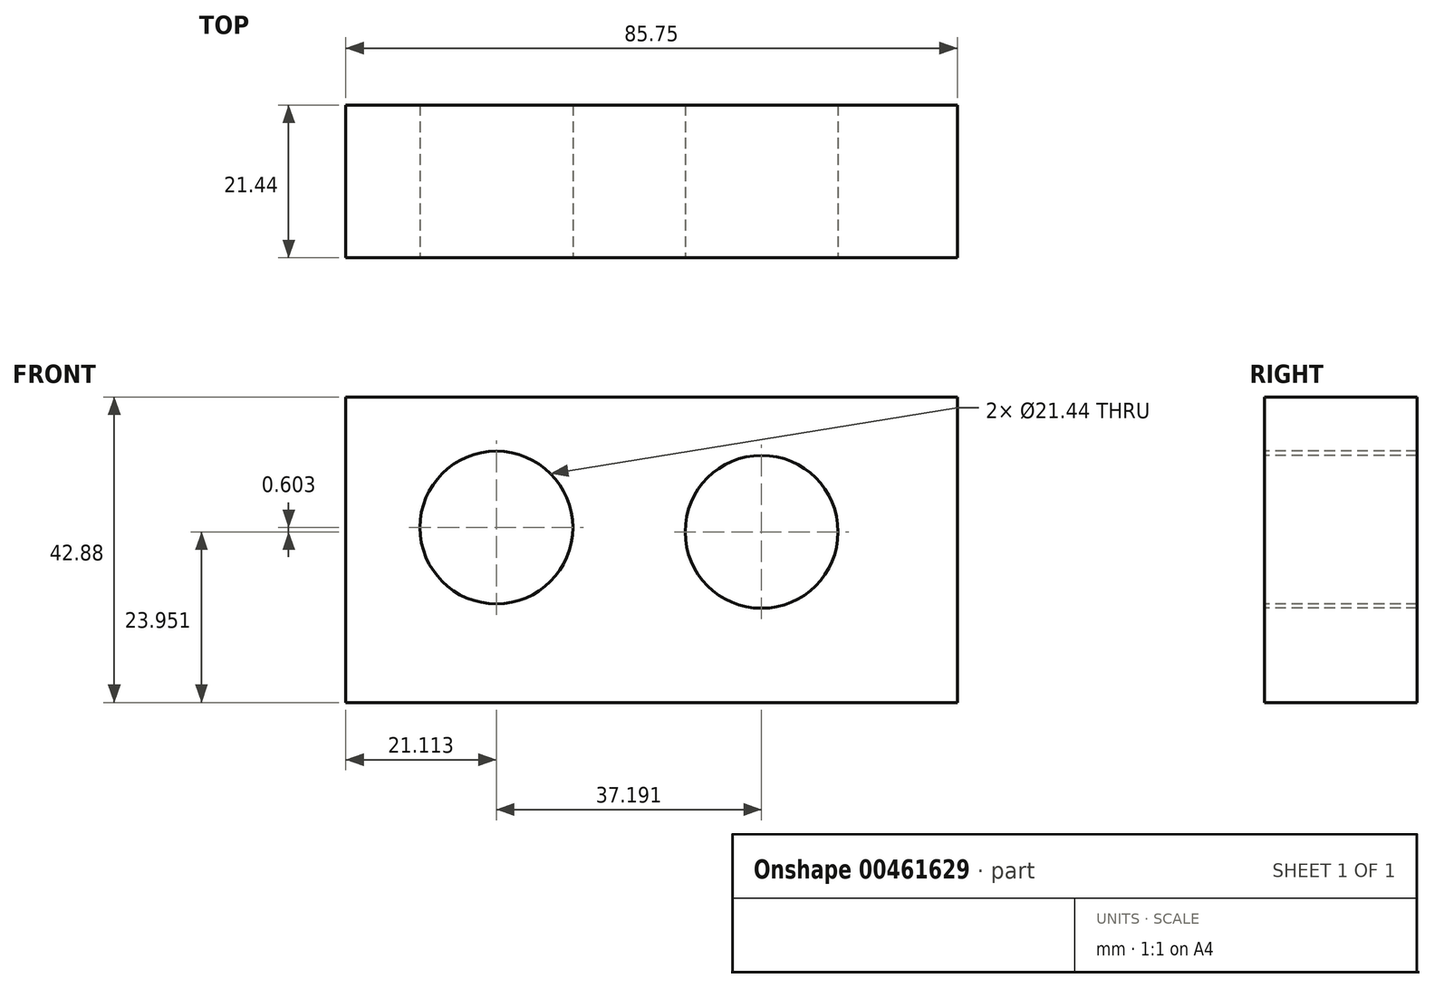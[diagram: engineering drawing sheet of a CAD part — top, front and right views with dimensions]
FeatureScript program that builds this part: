
annotation { "Feature Type Name" : "Feature", "Feature Type Description" : "" }
export const myFeature = defineFeature(function(context is Context, id is Id, definition is map)
    precondition{}
    {
        {
            var Q0;
            Q0=qCreatedBy(makeId("Front.planeOp"),FACE);
            var sketch = newSketch(context, id + "F0", { "sketchPlane" : qUnion([Q0])});
            skLineSegment(sketch, "E0.bottom", {"start": v(-34.18, 21.14) * mm, "end": v(51.57, 21.14) * mm});
            skLineSegment(sketch, "E0.top", {"start": v(-34.18, -21.74) * mm, "end": v(51.57, -21.74) * mm});
            skLineSegment(sketch, "E0.left", {"start": v(-34.18, 21.14) * mm, "end": v(-34.18, -21.74) * mm});
            skLineSegment(sketch, "E0.right", {"start": v(51.57, 21.14) * mm, "end": v(51.57, -21.74) * mm});
            skSolve(sketch);
        }
        {
            var Q0;
            Q0 = qSketchRegion(id + "F0", true);
            extrude(context, id + "F1", {"entities" : qUnion([Q0]), "depth" : 21.44 * mm});
        }
        {
            var Q0;
            Q0=makeQuery(id+"F1.opExtrude","CAP_FACE",FACE,{"disambiguationData":[OSD([sQuery(id+"F0.wireOp",EDGE,"E0.bottom"),sQuery(id+"F0.wireOp",EDGE,"E0.top"),sQuery(id+"F0.wireOp",EDGE,"E0.left"),sQuery(id+"F0.wireOp",EDGE,"E0.right")])],"isStart":false});
            var sketch = newSketch(context, id + "F2", { "sketchPlane" : qUnion([Q0])});
            skCircle(sketch, "E1", {"center": v(-13.07, 2.81) * mm, "radius": 10.72 * mm});
            skSolve(sketch);
        }
        {
            var Q0;
            Q0 = qSketchRegion(id + "F2", true);
            extrude(context, id + "F3", {"entities" : qUnion([Q0]), "operationType" : NewBodyOperationType.REMOVE, "oppositeDirection" : true, "depth" : 32.5 * mm});
        }
        {
            var Q0;
            Q0=makeQuery(id+"F1.opExtrude","CAP_FACE",FACE,{"disambiguationData":[OSD([sQuery(id+"F0.wireOp",EDGE,"E0.bottom"),sQuery(id+"F0.wireOp",EDGE,"E0.top"),sQuery(id+"F0.wireOp",EDGE,"E0.left"),sQuery(id+"F0.wireOp",EDGE,"E0.right")])],"isStart":false});
            var sketch = newSketch(context, id + "F4", { "sketchPlane" : qUnion([Q0])});
            skCircle(sketch, "E2", {"center": v(24.12, 2.21) * mm, "radius": 10.72 * mm});
            skSolve(sketch);
        }
        {
            var Q0;
            Q0 = qSketchRegion(id + "F4", true);
            extrude(context, id + "F5", {"entities" : qUnion([Q0]), "operationType" : NewBodyOperationType.REMOVE, "oppositeDirection" : true, "depth" : 21.44 * mm});
        }
    });
